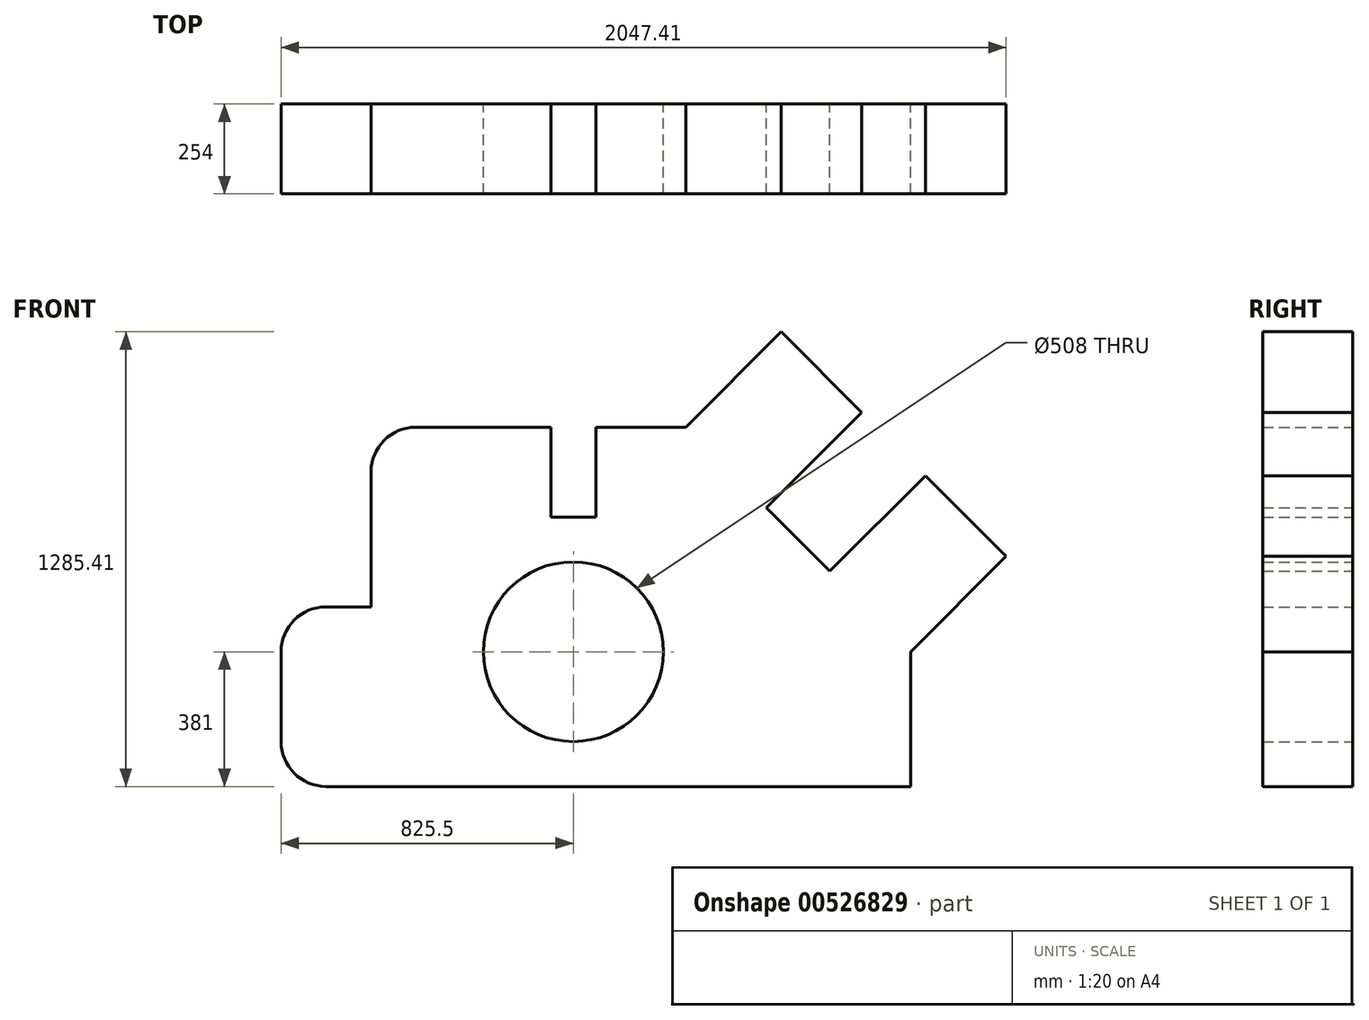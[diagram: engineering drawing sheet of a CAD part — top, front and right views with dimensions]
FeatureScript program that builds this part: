
annotation { "Feature Type Name" : "Feature", "Feature Type Description" : "" }
export const myFeature = defineFeature(function(context is Context, id is Id, definition is map)
    precondition{}
    {
        {
            var Q0;
            Q0=qCreatedBy(makeId("Front.planeOp"),FACE);
            var sketch = newSketch(context, id + "F0", { "sketchPlane" : qUnion([Q0])});
            skLineSegment(sketch, "E0", {"start": v(127, 0) * mm, "end": v(1778, 0) * mm});
            skLineSegment(sketch, "E1", {"start": v(1778, 0) * mm, "end": v(1778, 381) * mm});
            skLineSegment(sketch, "E2", {"start": v(0, 127) * mm, "end": v(0, 381) * mm});
            skCircle(sketch, "E3", {"center": v(825.5, 381) * mm, "radius": 254 * mm});
            skLineSegment(sketch, "E4", {"start": v(127, 508) * mm, "end": v(254, 508) * mm});
            skLineSegment(sketch, "E5", {"start": v(254, 508) * mm, "end": v(254, 889) * mm});
            skLineSegment(sketch, "E6", {"start": v(381, 1016) * mm, "end": v(762, 1016) * mm});
            skLineSegment(sketch, "E7", {"start": v(762, 1016) * mm, "end": v(762, 762) * mm});
            skLineSegment(sketch, "E8", {"start": v(762, 762) * mm, "end": v(889, 762) * mm});
            skLineSegment(sketch, "E9", {"start": v(889, 762) * mm, "end": v(889, 1016) * mm});
            skLineSegment(sketch, "E10", {"start": v(889, 1016) * mm, "end": v(1143, 1016) * mm});
            skLineSegment(sketch, "E11", {"start": v(1778, 381) * mm, "end": v(2047.4, 650.4) * mm});
            skLineSegment(sketch, "E12", {"start": v(2047.4, 650.4) * mm, "end": v(1819.71, 878.1) * mm});
            skLineSegment(sketch, "E13", {"start": v(1819.71, 878.1) * mm, "end": v(1550.3, 608.7) * mm});
            skLineSegment(sketch, "E14", {"start": v(1550.3, 608.7) * mm, "end": v(1370.7, 788.3) * mm});
            skLineSegment(sketch, "E15", {"start": v(1370.7, 788.3) * mm, "end": v(1640.1, 1057.71) * mm});
            skLineSegment(sketch, "E16", {"start": v(1640.1, 1057.71) * mm, "end": v(1412.4, 1285.4) * mm});
            skLineSegment(sketch, "E17", {"start": v(1143, 1016) * mm, "end": v(1412.4, 1285.4) * mm});
            skPoint(sketch, "E18.visualSharp", {"position": v(0, 0) * mm});
            skArc(sketch, "E18.filletArc", {"start": v(0, 127) * mm, "mid": v(37.2, 37.2) * mm, "end": v(127, 0) * mm});
            skPoint(sketch, "E19.visualSharp", {"position": v(0, 508) * mm});
            skArc(sketch, "E19.filletArc", {"start": v(127, 508) * mm, "mid": v(37.2, 470.8) * mm, "end": v(0, 381) * mm});
            skPoint(sketch, "E20.visualSharp", {"position": v(254, 1016) * mm});
            skArc(sketch, "E20.filletArc", {"start": v(381, 1016) * mm, "mid": v(291.2, 978.8) * mm, "end": v(254, 889) * mm});
            skSolve(sketch);
        }
        {
            var Q0;
            Q0=makeQuery(id+"F0.imprint","IMPRINT",FACE,{"disambiguationData":[TD([[makeQuery(id+"F0.imprint","IMPRINT",EDGE,{"derivedFrom":sQuery(id+"F0.wireOp",EDGE,"E0")}),1.0]])]});
            extrude(context, id + "F1", {"entities" : qUnion([Q0]), "depth" : 254 * mm, "offsetDistance" : 25.4 * mm});
        }
    });
